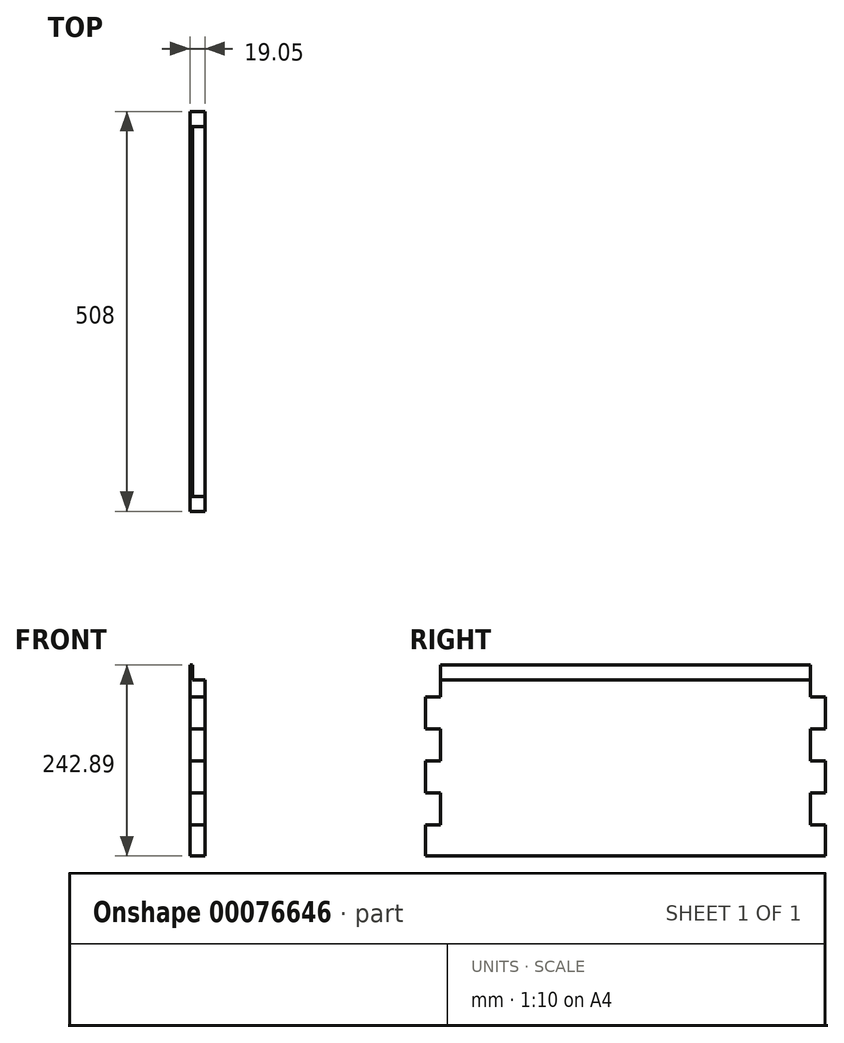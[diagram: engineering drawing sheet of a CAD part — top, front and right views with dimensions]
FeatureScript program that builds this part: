
annotation { "Feature Type Name" : "Feature", "Feature Type Description" : "" }
export const myFeature = defineFeature(function(context is Context, id is Id, definition is map)
    precondition{}
    {
        {
            var Q0;
            Q0=qCreatedBy(makeId("Right.planeOp"),FACE);
            var sketch = newSketch(context, id + "F0", { "sketchPlane" : qUnion([Q0])});
            skLineSegment(sketch, "E0.top", {"start": v(-618.08, -133.37) * mm, "end": v(-599.03, -133.37) * mm});
            skLineSegment(sketch, "E0.right", {"start": v(-599.03, -92.73) * mm, "end": v(-599.03, -133.37) * mm});
            skLineSegment(sketch, "E1.top", {"start": v(-618.08, -174.01) * mm, "end": v(-599.03, -174.01) * mm});
            skLineSegment(sketch, "E1.left", {"start": v(-618.08, -133.37) * mm, "end": v(-618.08, -174.01) * mm});
            skLineSegment(sketch, "E2.top", {"start": v(-618.08, -214.65) * mm, "end": v(-599.03, -214.65) * mm});
            skLineSegment(sketch, "E2.right", {"start": v(-599.03, -174.01) * mm, "end": v(-599.03, -214.65) * mm});
            skLineSegment(sketch, "E3.top", {"start": v(-618.08, -255.3) * mm, "end": v(-599.03, -255.3) * mm});
            skLineSegment(sketch, "E3.left", {"start": v(-618.08, -214.65) * mm, "end": v(-618.08, -255.3) * mm});
            skLineSegment(sketch, "E4.top", {"start": v(-618.08, -295.93) * mm, "end": v(-599.03, -295.93) * mm});
            skLineSegment(sketch, "E4.right", {"start": v(-599.03, -255.3) * mm, "end": v(-599.03, -295.93) * mm});
            skLineSegment(sketch, "E5.top", {"start": v(-618.08, -335.62) * mm, "end": v(-599.03, -335.62) * mm});
            skLineSegment(sketch, "E5.left", {"start": v(-618.08, -295.93) * mm, "end": v(-618.08, -335.62) * mm});
            skLineSegment(sketch, "E6", {"start": v(-364.08, -92.73) * mm, "end": v(-364.08, -335.62) * mm, "construction": true});
            skLineSegment(sketch, "E7.MirrorCS", {"start": v(-110.08, -295.93) * mm, "end": v(-129.13, -295.93) * mm});
            skLineSegment(sketch, "E8.MirrorCS", {"start": v(-110.08, -174.01) * mm, "end": v(-129.13, -174.01) * mm});
            skLineSegment(sketch, "E9.MirrorCS", {"start": v(-110.08, -133.37) * mm, "end": v(-129.13, -133.37) * mm});
            skLineSegment(sketch, "E10.MirrorCS", {"start": v(-110.08, -214.65) * mm, "end": v(-129.13, -214.65) * mm});
            skLineSegment(sketch, "E11.MirrorCS", {"start": v(-110.08, -255.3) * mm, "end": v(-129.13, -255.3) * mm});
            skLineSegment(sketch, "E12.MirrorCS", {"start": v(-110.08, -295.93) * mm, "end": v(-110.08, -335.62) * mm});
            skLineSegment(sketch, "E13.MirrorCS", {"start": v(-110.08, -335.62) * mm, "end": v(-129.13, -335.62) * mm});
            skLineSegment(sketch, "E14.MirrorCS", {"start": v(-110.08, -214.65) * mm, "end": v(-110.08, -255.3) * mm});
            skLineSegment(sketch, "E15.MirrorCS", {"start": v(-110.08, -133.37) * mm, "end": v(-110.08, -174.01) * mm});
            skLineSegment(sketch, "E16.MirrorCS", {"start": v(-129.13, -255.3) * mm, "end": v(-129.13, -295.93) * mm});
            skLineSegment(sketch, "E17.MirrorCS", {"start": v(-129.13, -174.01) * mm, "end": v(-129.13, -214.65) * mm});
            skLineSegment(sketch, "E18.MirrorCS", {"start": v(-129.13, -92.73) * mm, "end": v(-129.13, -133.37) * mm});
            skLineSegment(sketch, "E19", {"start": v(-129.13, -92.73) * mm, "end": v(-599.03, -92.73) * mm});
            skLineSegment(sketch, "E20", {"start": v(-129.13, -335.62) * mm, "end": v(-599.03, -335.62) * mm});
            skSolve(sketch);
        }
        {
            var Q0;
            Q0=makeQuery(id+"F0.imprint","IMPRINT",FACE,{"disambiguationData":[TD([[makeQuery(id+"F0.imprint","IMPRINT",EDGE,{"derivedFrom":sQuery(id+"F0.wireOp",EDGE,"E0.right")}),1.0]])]});
            extrude(context, id + "F1", {"entities" : qUnion([Q0]), "depth" : 19.05 * mm});
        }
        {
            var Q0;
            Q0=makeQuery(id+"F1.opExtrude","CAP_FACE",FACE,{"disambiguationData":[OSD([sQuery(id+"F0.wireOp",EDGE,"E0.right"),sQuery(id+"F0.wireOp",EDGE,"E0.top"),sQuery(id+"F0.wireOp",EDGE,"E1.left"),sQuery(id+"F0.wireOp",EDGE,"E1.top"),sQuery(id+"F0.wireOp",EDGE,"E2.right"),sQuery(id+"F0.wireOp",EDGE,"E2.top"),sQuery(id+"F0.wireOp",EDGE,"E3.left"),sQuery(id+"F0.wireOp",EDGE,"E3.top"),sQuery(id+"F0.wireOp",EDGE,"E4.right"),sQuery(id+"F0.wireOp",EDGE,"E4.top"),sQuery(id+"F0.wireOp",EDGE,"E5.top"),sQuery(id+"F0.wireOp",EDGE,"E5.left"),sQuery(id+"F0.wireOp",EDGE,"E12.MirrorCS"),sQuery(id+"F0.wireOp",EDGE,"E13.MirrorCS"),sQuery(id+"F0.wireOp",EDGE,"E14.MirrorCS"),sQuery(id+"F0.wireOp",EDGE,"E7.MirrorCS"),sQuery(id+"F0.wireOp",EDGE,"E8.MirrorCS"),sQuery(id+"F0.wireOp",EDGE,"E9.MirrorCS"),sQuery(id+"F0.wireOp",EDGE,"E15.MirrorCS"),sQuery(id+"F0.wireOp",EDGE,"E11.MirrorCS"),sQuery(id+"F0.wireOp",EDGE,"E10.MirrorCS"),sQuery(id+"F0.wireOp",EDGE,"E16.MirrorCS"),sQuery(id+"F0.wireOp",EDGE,"E17.MirrorCS"),sQuery(id+"F0.wireOp",EDGE,"E18.MirrorCS"),sQuery(id+"F0.wireOp",EDGE,"E19"),sQuery(id+"F0.wireOp",EDGE,"E20")])],"isStart":false});
            var sketch = newSketch(context, id + "F2", { "sketchPlane" : qUnion([Q0])});
            skLineSegment(sketch, "E21", {"start": v(-599.03, -92.73) * mm, "end": v(-599.03, -111.78) * mm});
            skLineSegment(sketch, "E22", {"start": v(-599.03, -111.78) * mm, "end": v(-129.13, -111.78) * mm});
            skLineSegment(sketch, "E23", {"start": v(-129.13, -111.78) * mm, "end": v(-129.13, -92.73) * mm});
            skLineSegment(sketch, "E24", {"start": v(-129.13, -92.73) * mm, "end": v(-599.03, -92.73) * mm});
            skSolve(sketch);
        }
        {
            var Q0;
            Q0 = qSketchRegion(id + "F2", true);
            extrude(context, id + "F3", {"entities" : qUnion([Q0]), "operationType" : NewBodyOperationType.REMOVE, "oppositeDirection" : true, "depth" : 15.88 * mm});
        }
    });
